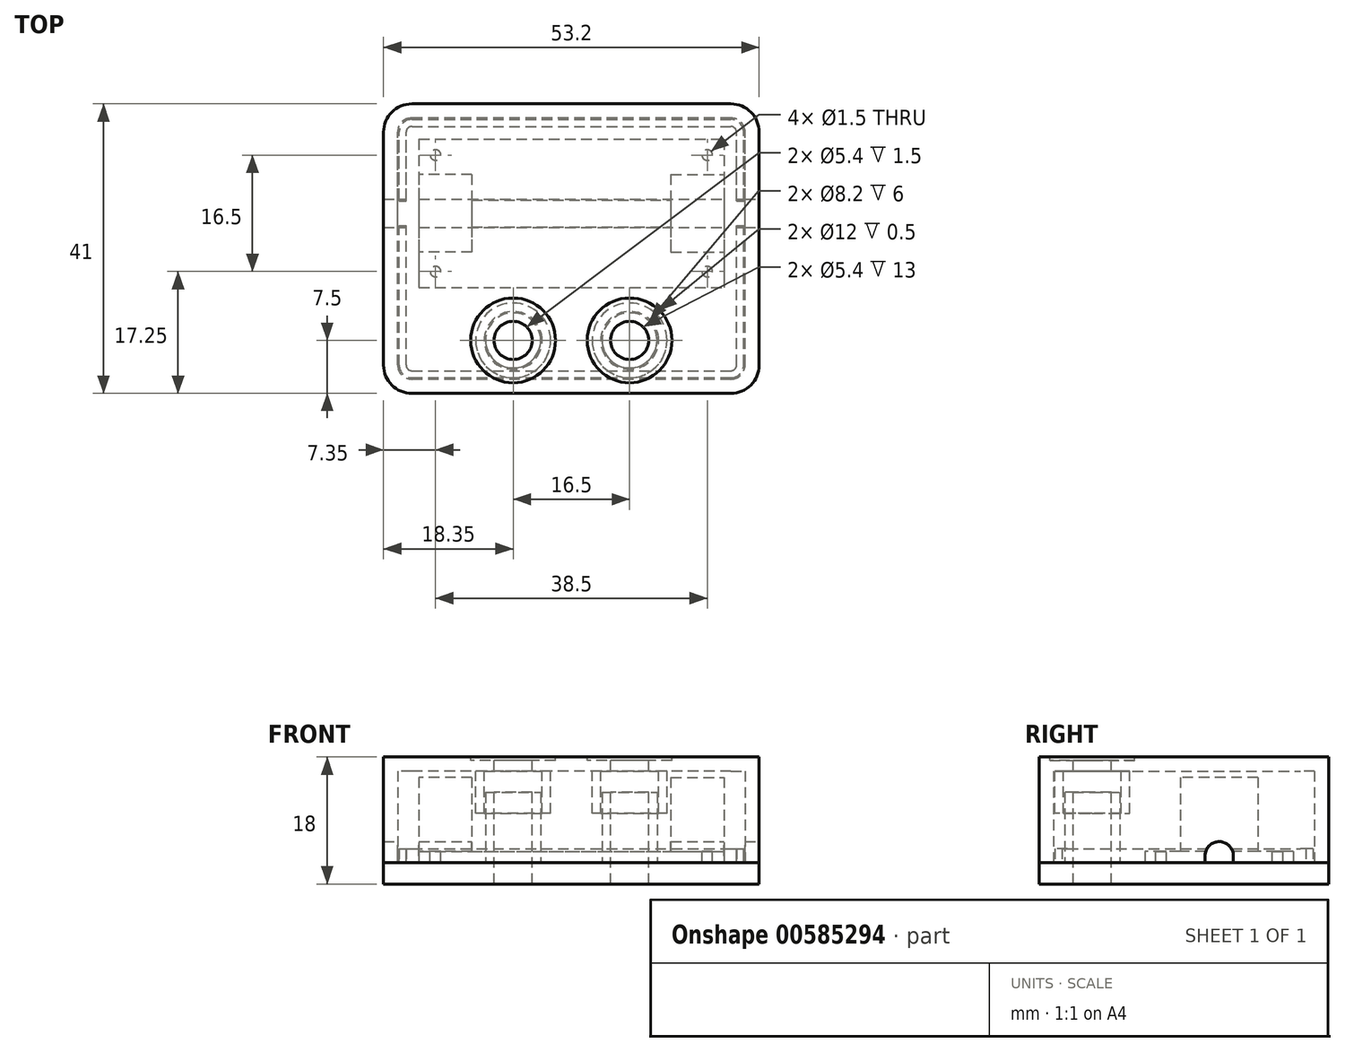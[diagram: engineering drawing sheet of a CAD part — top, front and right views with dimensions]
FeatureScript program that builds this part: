
annotation { "Feature Type Name" : "Feature", "Feature Type Description" : "" }
export const myFeature = defineFeature(function(context is Context, id is Id, definition is map)
    precondition{}
    {
        {
            var Q0;
            Q0=qCreatedBy(makeId("Top.planeOp"),FACE);
            var sketch = newSketch(context, id + "F0", { "sketchPlane" : qUnion([Q0])});
            skLineSegment(sketch, "E0.bottom", {"start": v(-21.6, 10.5) * mm, "end": v(21.6, 10.5) * mm});
            skLineSegment(sketch, "E0.top", {"start": v(-21.6, -10.5) * mm, "end": v(21.6, -10.5) * mm});
            skLineSegment(sketch, "E0.left", {"start": v(-21.6, 10.5) * mm, "end": v(-21.6, -10.5) * mm});
            skLineSegment(sketch, "E0.right", {"start": v(21.6, 10.5) * mm, "end": v(21.6, -10.5) * mm});
            skPoint(sketch, "E0.middle", {"position": v(0, 0) * mm});
            skSolve(sketch);
        }
        {
            var Q0;
            Q0=makeQuery(id+"F0.imprint","IMPRINT",FACE,{"disambiguationData":[TD([[makeQuery(id+"F0.imprint","IMPRINT",EDGE,{"derivedFrom":sQuery(id+"F0.wireOp",EDGE,"E0.bottom")}),-1.0]])]});
            extrude(context, id + "F1", {"entities" : qUnion([Q0]), "depth" : 1.6 * mm, "offsetDistance" : 25 * mm});
        }
        {
            var Q0;
            Q0=makeQuery(id+"F1.opExtrude","CAP_FACE",FACE,{"disambiguationData":[OSD([sQuery(id+"F0.wireOp",EDGE,"E0.bottom"),sQuery(id+"F0.wireOp",EDGE,"E0.top"),sQuery(id+"F0.wireOp",EDGE,"E0.left"),sQuery(id+"F0.wireOp",EDGE,"E0.right")])],"isStart":false});
            var sketch = newSketch(context, id + "F2", { "sketchPlane" : qUnion([Q0])});
            skLineSegment(sketch, "E1.bottom", {"start": v(-19.25, 8.25) * mm, "end": v(19.25, 8.25) * mm, "construction": true});
            skLineSegment(sketch, "E1.top", {"start": v(-19.25, -8.25) * mm, "end": v(19.25, -8.25) * mm, "construction": true});
            skLineSegment(sketch, "E1.left", {"start": v(-19.25, 8.25) * mm, "end": v(-19.25, -8.25) * mm, "construction": true});
            skLineSegment(sketch, "E1.right", {"start": v(19.25, 8.25) * mm, "end": v(19.25, -8.25) * mm, "construction": true});
            skPoint(sketch, "E1.middle", {"position": v(0, 0) * mm});
            skCircle(sketch, "E2", {"center": v(-19.25, 8.25) * mm, "radius": 0.75 * mm});
            skCircle(sketch, "E3", {"center": v(-19.25, -8.25) * mm, "radius": 0.75 * mm});
            skCircle(sketch, "E4", {"center": v(19.25, 8.25) * mm, "radius": 0.75 * mm});
            skCircle(sketch, "E5", {"center": v(19.25, -8.25) * mm, "radius": 0.75 * mm});
            skSolve(sketch);
        }
        {
            var Q0;
            Q0 = qSketchRegion(id + "F2", true);
            extrude(context, id + "F3", {"entities" : qUnion([Q0]), "operationType" : NewBodyOperationType.REMOVE, "oppositeDirection" : true, "depth" : 25 * mm, "offsetDistance" : 25 * mm});
        }
        {
            var Q0;
            Q0=makeQuery(id+"F1.opExtrude","CAP_FACE",FACE,{"disambiguationData":[OSD([sQuery(id+"F0.wireOp",EDGE,"E0.bottom"),sQuery(id+"F0.wireOp",EDGE,"E0.top"),sQuery(id+"F0.wireOp",EDGE,"E0.left"),sQuery(id+"F0.wireOp",EDGE,"E0.right")])],"isStart":false});
            var sketch = newSketch(context, id + "F4", { "sketchPlane" : qUnion([Q0])});
            skLineSegment(sketch, "E6.bottom", {"start": v(14.1, 5.5) * mm, "end": v(21.6, 5.5) * mm});
            skLineSegment(sketch, "E6.top", {"start": v(14.1, -5.5) * mm, "end": v(21.6, -5.5) * mm});
            skLineSegment(sketch, "E6.left", {"start": v(14.1, 5.5) * mm, "end": v(14.1, -5.5) * mm});
            skLineSegment(sketch, "E6.right", {"start": v(21.6, 5.5) * mm, "end": v(21.6, -5.5) * mm});
            skLineSegment(sketch, "E7.MirrorCS", {"start": v(-14.1, 5.5) * mm, "end": v(-21.6, 5.5) * mm});
            skLineSegment(sketch, "E8.MirrorCS", {"start": v(-14.1, -5.5) * mm, "end": v(-21.6, -5.5) * mm});
            skLineSegment(sketch, "E9.MirrorCS", {"start": v(-14.1, 5.5) * mm, "end": v(-14.1, -5.5) * mm});
            skLineSegment(sketch, "E10.MirrorCS", {"start": v(-21.6, 5.5) * mm, "end": v(-21.6, -5.5) * mm});
            skSolve(sketch);
        }
        {
            var Q0;
            Q0 = qSketchRegion(id + "F4", true);
            extrude(context, id + "F5", {"entities" : qUnion([Q0]), "operationType" : NewBodyOperationType.ADD, "depth" : 10.5 * mm, "offsetDistance" : 25 * mm});
        }
        {
            var Q0;
            Q0=makeQuery(id+"F1.opExtrude","CAP_FACE",FACE,{"disambiguationData":[OSD([sQuery(id+"F0.wireOp",EDGE,"E0.bottom"),sQuery(id+"F0.wireOp",EDGE,"E0.top"),sQuery(id+"F0.wireOp",EDGE,"E0.left"),sQuery(id+"F0.wireOp",EDGE,"E0.right")])],"isStart":true});
            var sketch = newSketch(context, id + "F6", { "sketchPlane" : qUnion([Q0])});
            skLineSegment(sketch, "E11.bottom", {"start": v(-26.6, 25.5) * mm, "end": v(26.6, 25.5) * mm});
            skLineSegment(sketch, "E11.top", {"start": v(-26.6, -15.5) * mm, "end": v(26.6, -15.5) * mm});
            skLineSegment(sketch, "E11.left", {"start": v(-26.6, 25.5) * mm, "end": v(-26.6, -15.5) * mm});
            skLineSegment(sketch, "E11.right", {"start": v(26.6, 25.5) * mm, "end": v(26.6, -15.5) * mm});
            skSolve(sketch);
        }
        {
            var Q0;
            Q0 = qSketchRegion(id + "F6", true);
            extrude(context, id + "F7", {"entities" : qUnion([Q0]), "depth" : 3 * mm, "offsetDistance" : 25 * mm});
        }
        {
            var Q0;
            Q0=makeQuery(id+"F7.opExtrude","CAP_FACE",FACE,{"disambiguationData":[OSD([sQuery(id+"F6.wireOp",EDGE,"E11.bottom"),sQuery(id+"F6.wireOp",EDGE,"E11.top"),sQuery(id+"F6.wireOp",EDGE,"E11.left"),sQuery(id+"F6.wireOp",EDGE,"E11.right")])],"isStart":true});
            var sketch = newSketch(context, id + "F8", { "sketchPlane" : qUnion([Q0])});
            skCircle(sketch, "E12", {"center": v(-8.25, -18) * mm, "radius": 2.7 * mm});
            skCircle(sketch, "E13", {"center": v(8.25, -18) * mm, "radius": 2.7 * mm});
            skSolve(sketch);
        }
        {
            var Q0;
            Q0 = qSketchRegion(id + "F8", true);
            extrude(context, id + "F9", {"entities" : qUnion([Q0]), "operationType" : NewBodyOperationType.REMOVE, "oppositeDirection" : true, "depth" : 25 * mm, "offsetDistance" : 25 * mm});
        }
        {
            var Q0;
            Q0=makeQuery(id+"F7.opExtrude","CAP_FACE",FACE,{"disambiguationData":[OSD([sQuery(id+"F6.wireOp",EDGE,"E11.bottom"),sQuery(id+"F6.wireOp",EDGE,"E11.top"),sQuery(id+"F6.wireOp",EDGE,"E11.left"),sQuery(id+"F6.wireOp",EDGE,"E11.right")])],"isStart":true});
            var sketch = newSketch(context, id + "F10", { "sketchPlane" : qUnion([Q0])});
            skLineSegment(sketch, "E14.bottom", {"start": v(-26.6, 15.5) * mm, "end": v(26.6, 15.5) * mm});
            skLineSegment(sketch, "E14.top", {"start": v(-26.6, -25.5) * mm, "end": v(26.6, -25.5) * mm});
            skLineSegment(sketch, "E14.left", {"start": v(-26.6, 15.5) * mm, "end": v(-26.6, -25.5) * mm});
            skLineSegment(sketch, "E14.right", {"start": v(26.6, 15.5) * mm, "end": v(26.6, -25.5) * mm});
            skLineSegment(sketch, "E15.bottom", {"start": v(24.6, -23.5) * mm, "end": v(-24.6, -23.5) * mm});
            skLineSegment(sketch, "E15.top", {"start": v(24.6, 13.5) * mm, "end": v(-24.6, 13.5) * mm});
            skLineSegment(sketch, "E15.left", {"start": v(24.6, -23.5) * mm, "end": v(24.6, 13.5) * mm});
            skLineSegment(sketch, "E15.right", {"start": v(-24.6, -23.5) * mm, "end": v(-24.6, 13.5) * mm});
            skSolve(sketch);
        }
        {
            var Q0;
            Q0 = qSketchRegion(id + "F10", true);
            extrude(context, id + "F11", {"entities" : qUnion([Q0]), "depth" : 13 * mm, "offsetDistance" : 25 * mm});
        }
        {
            var Q0;
            Q0=makeQuery(id+"F11.opExtrude","SWEPT_EDGE",EDGE,{"disambiguationData":[OSD([sQuery(id+"F10.wireOp",EDGE,"E15.top"),sQuery(id+"F10.wireOp",EDGE,"E15.left")])]});
            var Q1;
            Q1=makeQuery(id+"F11.opExtrude","SWEPT_EDGE",EDGE,{"disambiguationData":[OSD([sQuery(id+"F10.wireOp",EDGE,"E15.bottom"),sQuery(id+"F10.wireOp",EDGE,"E15.left")])]});
            var Q2;
            Q2=makeQuery(id+"F11.opExtrude","SWEPT_EDGE",EDGE,{"disambiguationData":[OSD([sQuery(id+"F10.wireOp",EDGE,"E15.bottom"),sQuery(id+"F10.wireOp",EDGE,"E15.right")])]});
            var Q3;
            Q3=makeQuery(id+"F11.opExtrude","SWEPT_EDGE",EDGE,{"disambiguationData":[OSD([sQuery(id+"F10.wireOp",EDGE,"E15.top"),sQuery(id+"F10.wireOp",EDGE,"E15.right")])]});
            fillet(context, id + "F12", {"entities" : qUnion([Q0, Q1, Q2, Q3]), "radius" : 2 * mm, "tangentPropagation" : true, "allowEdgeOverflow" : false});
        }
        {
            var Q0;
            Q0=makeQuery(id+"F11.opExtrude","SWEPT_EDGE",EDGE,{"disambiguationData":[OSD([sQuery(id+"F10.wireOp",EDGE,"E14.bottom"),sQuery(id+"F10.wireOp",EDGE,"E14.right")])]});
            var Q1;
            Q1=makeQuery(id+"F7.opExtrude","SWEPT_EDGE",EDGE,{"disambiguationData":[OSD([sQuery(id+"F6.wireOp",EDGE,"E11.top"),sQuery(id+"F6.wireOp",EDGE,"E11.right")])]});
            var Q2;
            Q2=makeQuery(id+"F11.opExtrude","SWEPT_EDGE",EDGE,{"disambiguationData":[OSD([sQuery(id+"F10.wireOp",EDGE,"E14.bottom"),sQuery(id+"F10.wireOp",EDGE,"E14.left")])]});
            var Q3;
            Q3=makeQuery(id+"F7.opExtrude","SWEPT_EDGE",EDGE,{"disambiguationData":[OSD([sQuery(id+"F6.wireOp",EDGE,"E11.top"),sQuery(id+"F6.wireOp",EDGE,"E11.left")])]});
            var Q4;
            Q4=makeQuery(id+"F11.opExtrude","SWEPT_EDGE",EDGE,{"disambiguationData":[OSD([sQuery(id+"F10.wireOp",EDGE,"E14.top"),sQuery(id+"F10.wireOp",EDGE,"E14.left")])]});
            var Q5;
            Q5=makeQuery(id+"F7.opExtrude","SWEPT_EDGE",EDGE,{"disambiguationData":[OSD([sQuery(id+"F6.wireOp",EDGE,"E11.bottom"),sQuery(id+"F6.wireOp",EDGE,"E11.left")])]});
            var Q6;
            Q6=makeQuery(id+"F11.opExtrude","SWEPT_EDGE",EDGE,{"disambiguationData":[OSD([sQuery(id+"F10.wireOp",EDGE,"E14.top"),sQuery(id+"F10.wireOp",EDGE,"E14.right")])]});
            var Q7;
            Q7=makeQuery(id+"F7.opExtrude","SWEPT_EDGE",EDGE,{"disambiguationData":[OSD([sQuery(id+"F6.wireOp",EDGE,"E11.bottom"),sQuery(id+"F6.wireOp",EDGE,"E11.right")])]});
            fillet(context, id + "F13", {"entities" : qUnion([Q0, Q1, Q2, Q3, Q4, Q5, Q6, Q7]), "radius" : 4 * mm, "tangentPropagation" : true, "allowEdgeOverflow" : false});
        }
        {
            var Q0;
            Q0=makeQuery(id+"F11.opExtrude","CAP_FACE",FACE,{"disambiguationData":[OSD([sQuery(id+"F10.wireOp",EDGE,"E14.bottom"),sQuery(id+"F10.wireOp",EDGE,"E14.top"),sQuery(id+"F10.wireOp",EDGE,"E14.left"),sQuery(id+"F10.wireOp",EDGE,"E14.right"),sQuery(id+"F10.wireOp",EDGE,"E15.bottom"),sQuery(id+"F10.wireOp",EDGE,"E15.top"),sQuery(id+"F10.wireOp",EDGE,"E15.left"),sQuery(id+"F10.wireOp",EDGE,"E15.right")])],"isStart":false});
            var sketch = newSketch(context, id + "F14", { "sketchPlane" : qUnion([Q0])});
            skArc(sketch, "E16.0", {"start": v(-26.6, -21.5) * mm, "mid": v(-25.43, -24.33) * mm, "end": v(-22.6, -25.5) * mm});
            skLineSegment(sketch, "E16.1", {"start": v(-26.6, -21.5) * mm, "end": v(-26.6, 11.5) * mm});
            skLineSegment(sketch, "E16.2", {"start": v(-22.6, -25.5) * mm, "end": v(22.6, -25.5) * mm});
            skArc(sketch, "E16.3", {"start": v(-22.6, 15.5) * mm, "mid": v(-25.43, 14.33) * mm, "end": v(-26.6, 11.5) * mm});
            skArc(sketch, "E16.4", {"start": v(22.6, -25.5) * mm, "mid": v(25.43, -24.33) * mm, "end": v(26.6, -21.5) * mm});
            skLineSegment(sketch, "E16.5", {"start": v(26.6, -21.5) * mm, "end": v(26.6, 11.5) * mm});
            skArc(sketch, "E16.6", {"start": v(26.6, 11.5) * mm, "mid": v(25.43, 14.33) * mm, "end": v(22.6, 15.5) * mm});
            skLineSegment(sketch, "E16.7", {"start": v(-22.6, 15.5) * mm, "end": v(22.6, 15.5) * mm});
            skSolve(sketch);
        }
        {
            var Q0;
            Q0 = qSketchRegion(id + "F14", true);
            extrude(context, id + "F15", {"entities" : qUnion([Q0]), "operationType" : NewBodyOperationType.ADD, "depth" : 2 * mm, "offsetDistance" : 25 * mm});
        }
        {
            var Q0;
            Q0=makeQuery(id+"F7.opExtrude","CAP_FACE",FACE,{"disambiguationData":[OSD([sQuery(id+"F6.wireOp",EDGE,"E11.bottom"),sQuery(id+"F6.wireOp",EDGE,"E11.top"),sQuery(id+"F6.wireOp",EDGE,"E11.left"),sQuery(id+"F6.wireOp",EDGE,"E11.right")])],"isStart":true});
            var sketch = newSketch(context, id + "F16", { "sketchPlane" : qUnion([Q0])});
            skArc(sketch, "E17.0", {"start": v(-22.6, 13.3) * mm, "mid": v(-23.87, 12.77) * mm, "end": v(-24.4, 11.5) * mm});
            skLineSegment(sketch, "E17.1", {"start": v(-24.4, -21.5) * mm, "end": v(-24.4, 11.5) * mm});
            skLineSegment(sketch, "E17.2", {"start": v(-22.6, 13.3) * mm, "end": v(22.6, 13.3) * mm});
            skArc(sketch, "E17.3", {"start": v(-24.4, -21.5) * mm, "mid": v(-23.87, -22.77) * mm, "end": v(-22.6, -23.3) * mm});
            skArc(sketch, "E17.4", {"start": v(24.4, 11.5) * mm, "mid": v(23.87, 12.77) * mm, "end": v(22.6, 13.3) * mm});
            skLineSegment(sketch, "E17.5", {"start": v(24.4, -21.5) * mm, "end": v(24.4, 11.5) * mm});
            skArc(sketch, "E17.6", {"start": v(22.6, -23.3) * mm, "mid": v(23.87, -22.77) * mm, "end": v(24.4, -21.5) * mm});
            skLineSegment(sketch, "E17.7", {"start": v(-22.6, -23.3) * mm, "end": v(22.6, -23.3) * mm});
            skArc(sketch, "E18.0", {"start": v(-22.6, 12.3) * mm, "mid": v(-23.17, 12.07) * mm, "end": v(-23.4, 11.5) * mm});
            skLineSegment(sketch, "E18.1", {"start": v(-23.4, -21.5) * mm, "end": v(-23.4, 11.5) * mm});
            skLineSegment(sketch, "E18.2", {"start": v(-22.6, 12.3) * mm, "end": v(22.6, 12.3) * mm});
            skArc(sketch, "E18.3", {"start": v(-23.4, -21.5) * mm, "mid": v(-23.17, -22.07) * mm, "end": v(-22.6, -22.3) * mm});
            skArc(sketch, "E18.4", {"start": v(23.4, 11.5) * mm, "mid": v(23.17, 12.07) * mm, "end": v(22.6, 12.3) * mm});
            skLineSegment(sketch, "E18.5", {"start": v(23.4, -21.5) * mm, "end": v(23.4, 11.5) * mm});
            skArc(sketch, "E18.6", {"start": v(22.6, -22.3) * mm, "mid": v(23.17, -22.07) * mm, "end": v(23.4, -21.5) * mm});
            skLineSegment(sketch, "E18.7", {"start": v(-22.6, -22.3) * mm, "end": v(22.6, -22.3) * mm});
            skSolve(sketch);
        }
        {
            var Q0;
            Q0 = qSketchRegion(id + "F16", true);
            extrude(context, id + "F17", {"entities" : qUnion([Q0]), "operationType" : NewBodyOperationType.ADD, "depth" : 2 * mm, "offsetDistance" : 25 * mm});
        }
        {
            var Q0;
            Q0=makeQuery(id+"F17.boolean.opBoolean","SPLIT",FACE,{"disambiguationData":[TD([makeQuery(id+"F9.boolean.opBoolean","COPY",FACE,{"derivedFrom":makeQuery(id+"F9.opExtrude","SWEPT_FACE",FACE,{"disambiguationData":[OSD([sQuery(id+"F8.wireOp",EDGE,"E12")])]})})])],"derivedFrom":makeQuery(id+"F7.opExtrude","CAP_FACE",FACE,{"disambiguationData":[OSD([sQuery(id+"F6.wireOp",EDGE,"E11.bottom"),sQuery(id+"F6.wireOp",EDGE,"E11.top"),sQuery(id+"F6.wireOp",EDGE,"E11.left"),sQuery(id+"F6.wireOp",EDGE,"E11.right")])],"isStart":true})});
            var sketch = newSketch(context, id + "F18", { "sketchPlane" : qUnion([Q0])});
            skCircle(sketch, "E19", {"center": v(-8.25, -18) * mm, "radius": 3.9 * mm});
            skCircle(sketch, "E20", {"center": v(-8.25, -18) * mm, "radius": 2.7 * mm});
            skCircle(sketch, "E21.MirrorC", {"center": v(8.25, -18) * mm, "radius": 3.9 * mm});
            skCircle(sketch, "E22.MirrorC", {"center": v(8.25, -18) * mm, "radius": 2.7 * mm});
            skSolve(sketch);
        }
        {
            var Q0;
            Q0 = qSketchRegion(id + "F18", true);
            extrude(context, id + "F19", {"entities" : qUnion([Q0]), "operationType" : NewBodyOperationType.ADD, "depth" : 10 * mm, "offsetDistance" : 25 * mm});
        }
        {
            var Q0;
            Q0=makeQuery(id+"F15.opExtrude","CAP_FACE",FACE,{"disambiguationData":[OSD([sQuery(id+"F14.wireOp",EDGE,"E16.0"),sQuery(id+"F14.wireOp",EDGE,"E16.1"),sQuery(id+"F14.wireOp",EDGE,"E16.2"),sQuery(id+"F14.wireOp",EDGE,"E16.3"),sQuery(id+"F14.wireOp",EDGE,"E16.4"),sQuery(id+"F14.wireOp",EDGE,"E16.5"),sQuery(id+"F14.wireOp",EDGE,"E16.6"),sQuery(id+"F14.wireOp",EDGE,"E16.7")])],"isStart":false});
            var sketch = newSketch(context, id + "F20", { "sketchPlane" : qUnion([Q0])});
            skCircle(sketch, "E23.0", {"center": v(-8.25, -18) * mm, "radius": 2.7 * mm});
            skCircle(sketch, "E24.0", {"center": v(8.25, -18) * mm, "radius": 2.7 * mm});
            skSolve(sketch);
        }
        {
            var Q0;
            Q0 = qSketchRegion(id + "F20", true);
            extrude(context, id + "F21", {"entities" : qUnion([Q0]), "operationType" : NewBodyOperationType.REMOVE, "oppositeDirection" : true, "depth" : 25 * mm, "offsetDistance" : 25 * mm});
        }
        {
            var Q0;
            Q0=makeQuery(id+"F15.opExtrude","CAP_FACE",FACE,{"disambiguationData":[OSD([sQuery(id+"F14.wireOp",EDGE,"E16.0"),sQuery(id+"F14.wireOp",EDGE,"E16.1"),sQuery(id+"F14.wireOp",EDGE,"E16.2"),sQuery(id+"F14.wireOp",EDGE,"E16.3"),sQuery(id+"F14.wireOp",EDGE,"E16.4"),sQuery(id+"F14.wireOp",EDGE,"E16.5"),sQuery(id+"F14.wireOp",EDGE,"E16.6"),sQuery(id+"F14.wireOp",EDGE,"E16.7")])],"isStart":true});
            var sketch = newSketch(context, id + "F22", { "sketchPlane" : qUnion([Q0])});
            skCircle(sketch, "E25", {"center": v(-8.25, 18) * mm, "radius": 5.3 * mm});
            skCircle(sketch, "E26", {"center": v(-8.25, 18) * mm, "radius": 4.1 * mm});
            skCircle(sketch, "E27.MirrorC", {"center": v(8.25, 18) * mm, "radius": 4.1 * mm});
            skCircle(sketch, "E28.MirrorC", {"center": v(8.25, 18) * mm, "radius": 5.3 * mm});
            skSolve(sketch);
        }
        {
            var Q0;
            Q0 = qSketchRegion(id + "F22", true);
            extrude(context, id + "F23", {"entities" : qUnion([Q0]), "operationType" : NewBodyOperationType.ADD, "depth" : 6 * mm, "offsetDistance" : 25 * mm});
        }
        {
            var Q0;
            Q0=makeQuery(id+"F15.boolean.opBoolean","MERGE",FACE,{"derivedFrom":[makeQuery(id+"F11.opExtrude","SWEPT_FACE",FACE,{"disambiguationData":[OSD([sQuery(id+"F10.wireOp",EDGE,"E14.right")])]}),makeQuery(id+"F15.opExtrude","SWEPT_FACE",FACE,{"disambiguationData":[OSD([sQuery(id+"F14.wireOp",EDGE,"E16.5")])]})]});
            var sketch = newSketch(context, id + "F24", { "sketchPlane" : qUnion([Q0])});
            skLineSegment(sketch, "E29.bottom", {"start": v(0, 3) * mm, "end": v(0, 3) * mm});
            skLineSegment(sketch, "E29.top", {"start": v(-2, 0) * mm, "end": v(2, 0) * mm});
            skLineSegment(sketch, "E29.left", {"start": v(-2, 1) * mm, "end": v(-2, 0) * mm});
            skLineSegment(sketch, "E29.right", {"start": v(2, 1) * mm, "end": v(2, 0) * mm});
            skPoint(sketch, "E30.visualSharp", {"position": v(-2, 3) * mm});
            skArc(sketch, "E30.filletArc", {"start": v(0, 3) * mm, "mid": v(-1.41, 2.41) * mm, "end": v(-2, 1) * mm});
            skPoint(sketch, "E31.visualSharp", {"position": v(2, 3) * mm});
            skArc(sketch, "E31.filletArc", {"start": v(2, 1) * mm, "mid": v(1.41, 2.41) * mm, "end": v(0, 3) * mm});
            skSolve(sketch);
        }
        {
            var Q0;
            Q0 = qSketchRegion(id + "F24", true);
            extrude(context, id + "F25", {"entities" : qUnion([Q0]), "operationType" : NewBodyOperationType.REMOVE, "oppositeDirection" : true, "depth" : 63.4 * mm, "offsetDistance" : 25 * mm});
        }
        {
            var Q0;
            Q0=makeQuery(id+"F15.opExtrude","CAP_FACE",FACE,{"disambiguationData":[OSD([sQuery(id+"F14.wireOp",EDGE,"E16.0"),sQuery(id+"F14.wireOp",EDGE,"E16.1"),sQuery(id+"F14.wireOp",EDGE,"E16.2"),sQuery(id+"F14.wireOp",EDGE,"E16.3"),sQuery(id+"F14.wireOp",EDGE,"E16.4"),sQuery(id+"F14.wireOp",EDGE,"E16.5"),sQuery(id+"F14.wireOp",EDGE,"E16.6"),sQuery(id+"F14.wireOp",EDGE,"E16.7")])],"isStart":false});
            var sketch = newSketch(context, id + "F26", { "sketchPlane" : qUnion([Q0])});
            skCircle(sketch, "E32", {"center": v(-8.25, -18) * mm, "radius": 6 * mm});
            skCircle(sketch, "E33", {"center": v(8.25, -18) * mm, "radius": 6 * mm});
            skSolve(sketch);
        }
        {
            var Q0;
            Q0 = qSketchRegion(id + "F26", true);
            extrude(context, id + "F27", {"entities" : qUnion([Q0]), "operationType" : NewBodyOperationType.REMOVE, "oppositeDirection" : true, "depth" : 0.5 * mm, "offsetDistance" : 25 * mm});
        }
    });
